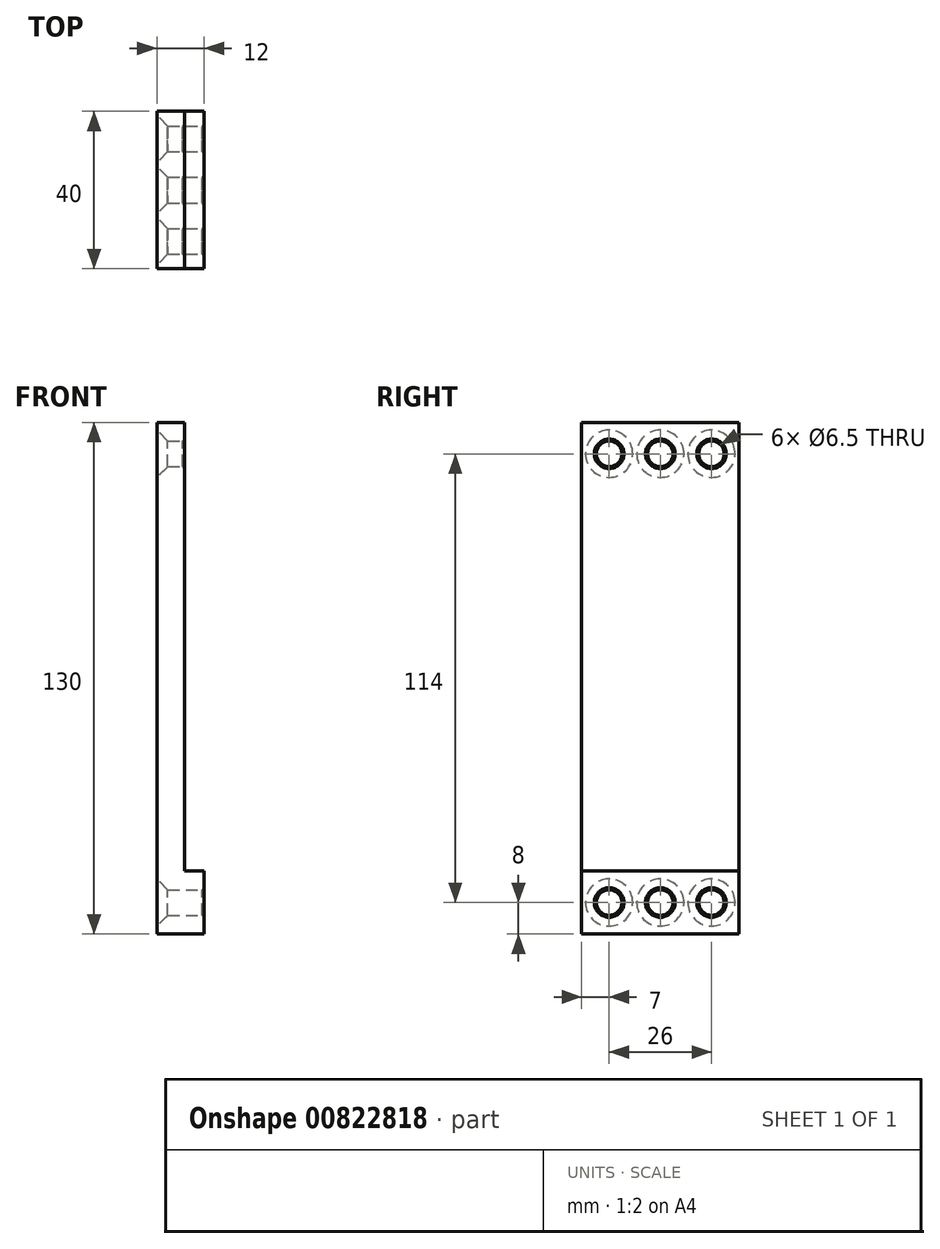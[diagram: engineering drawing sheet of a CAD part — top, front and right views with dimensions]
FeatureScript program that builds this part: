
annotation { "Feature Type Name" : "Feature", "Feature Type Description" : "" }
export const myFeature = defineFeature(function(context is Context, id is Id, definition is map)
    precondition{}
    {
        {
            var Q0;
            Q0=qCreatedBy(makeId("Right.planeOp"),FACE);
            var sketch = newSketch(context, id + "F0", { "sketchPlane" : qUnion([Q0])});
            skLineSegment(sketch, "E0", {"start": v(0, 0) * mm, "end": v(-13, 0) * mm, "construction": true});
            skLineSegment(sketch, "E1", {"start": v(0, 0) * mm, "end": v(0, 114) * mm, "construction": true});
            skLineSegment(sketch, "E2", {"start": v(0, 114) * mm, "end": v(-13, 114) * mm, "construction": true});
            skLineSegment(sketch, "E3", {"start": v(-13, 114) * mm, "end": v(-13, 0) * mm, "construction": true});
            skLineSegment(sketch, "E4.bottom", {"start": v(20, -8) * mm, "end": v(-20, -8) * mm});
            skLineSegment(sketch, "E4.top", {"start": v(20, 122) * mm, "end": v(-20, 122) * mm});
            skLineSegment(sketch, "E4.left", {"start": v(20, -8) * mm, "end": v(20, 122) * mm});
            skLineSegment(sketch, "E4.right", {"start": v(-20, -8) * mm, "end": v(-20, 122) * mm});
            skPoint(sketch, "E4.middle", {"position": v(0, 57) * mm});
            skCircle(sketch, "E5", {"center": v(0, 114) * mm, "radius": 3.25 * mm});
            skCircle(sketch, "E6", {"center": v(-13, 114) * mm, "radius": 3.25 * mm});
            skCircle(sketch, "E7", {"center": v(-13, 0) * mm, "radius": 3.25 * mm});
            skCircle(sketch, "E8", {"center": v(0, 0) * mm, "radius": 3.25 * mm});
            skCircle(sketch, "E9.MirrorC", {"center": v(13, 0) * mm, "radius": 3.25 * mm});
            skCircle(sketch, "E10.MirrorC", {"center": v(13, 114) * mm, "radius": 3.25 * mm});
            skSolve(sketch);
        }
        {
            var Q0;
            Q0 = qSketchRegion(id + "F0", true);
            extrude(context, id + "F1", {"entities" : qUnion([Q0]), "oppositeDirection" : true, "depth" : 7 * mm, "offsetDistance" : 25 * mm});
        }
        {
            var Q0;
            Q0=makeQuery(id+"F1.opExtrude","CAP_FACE",FACE,{"disambiguationData":[OSD([sQuery(id+"F0.wireOp",EDGE,"E4.bottom"),sQuery(id+"F0.wireOp",EDGE,"E4.top"),sQuery(id+"F0.wireOp",EDGE,"E4.left"),sQuery(id+"F0.wireOp",EDGE,"E4.right"),sQuery(id+"F0.wireOp",EDGE,"E5"),sQuery(id+"F0.wireOp",EDGE,"E6"),sQuery(id+"F0.wireOp",EDGE,"E7"),sQuery(id+"F0.wireOp",EDGE,"E8"),sQuery(id+"F0.wireOp",EDGE,"E9.MirrorC"),sQuery(id+"F0.wireOp",EDGE,"E10.MirrorC")])],"isStart":true});
            var sketch = newSketch(context, id + "F2", { "sketchPlane" : qUnion([Q0])});
            skCircle(sketch, "E11.0", {"center": v(-13, 0) * mm, "radius": 3.25 * mm});
            skLineSegment(sketch, "E12.0", {"start": v(20, -8) * mm, "end": v(-20, -8) * mm});
            skCircle(sketch, "E13.0", {"center": v(0, 0) * mm, "radius": 3.25 * mm});
            skCircle(sketch, "E14.0", {"center": v(13, 0) * mm, "radius": 3.25 * mm});
            skLineSegment(sketch, "E15", {"start": v(-20, -8) * mm, "end": v(-20, 8) * mm});
            skLineSegment(sketch, "E16", {"start": v(-20, 8) * mm, "end": v(20, 8) * mm});
            skLineSegment(sketch, "E17", {"start": v(20, 8) * mm, "end": v(20, -8) * mm});
            skSolve(sketch);
        }
        {
            var Q0;
            Q0 = qSketchRegion(id + "F2", true);
            extrude(context, id + "F3", {"entities" : qUnion([Q0]), "operationType" : NewBodyOperationType.ADD, "depth" : 5 * mm, "offsetDistance" : 25 * mm});
        }
        {
            var Q0;
            Q0=makeQuery(id+"F1.opExtrude","CAP_EDGE",EDGE,{"disambiguationData":[OSD([sQuery(id+"F0.wireOp",EDGE,"E7")])],"isStart":false});
            var Q1;
            Q1=makeQuery(id+"F1.opExtrude","CAP_EDGE",EDGE,{"disambiguationData":[OSD([sQuery(id+"F0.wireOp",EDGE,"E8")])],"isStart":false});
            var Q2;
            Q2=makeQuery(id+"F1.opExtrude","CAP_EDGE",EDGE,{"disambiguationData":[OSD([sQuery(id+"F0.wireOp",EDGE,"E9.MirrorC")])],"isStart":false});
            var Q3;
            Q3=makeQuery(id+"F1.opExtrude","CAP_EDGE",EDGE,{"disambiguationData":[OSD([sQuery(id+"F0.wireOp",EDGE,"E10.MirrorC")])],"isStart":false});
            var Q4;
            Q4=makeQuery(id+"F1.opExtrude","CAP_EDGE",EDGE,{"disambiguationData":[OSD([sQuery(id+"F0.wireOp",EDGE,"E5")])],"isStart":false});
            var Q5;
            Q5=makeQuery(id+"F1.opExtrude","CAP_EDGE",EDGE,{"disambiguationData":[OSD([sQuery(id+"F0.wireOp",EDGE,"E6")])],"isStart":false});
            chamfer(context, id + "F4", {"entities" : qUnion([Q0, Q1, Q2, Q3, Q4, Q5]), "width" : 2.75 * mm, "tangentPropagation" : true});
        }
        {
            var Q0;
            Q0=makeQuery(id+"F3.opExtrude","CAP_EDGE",EDGE,{"disambiguationData":[OSD([sQuery(id+"F2.wireOp",EDGE,"E11.0")])],"isStart":false});
            var Q1;
            Q1=makeQuery(id+"F3.opExtrude","CAP_EDGE",EDGE,{"disambiguationData":[OSD([sQuery(id+"F2.wireOp",EDGE,"E13.0")])],"isStart":false});
            var Q2;
            Q2=makeQuery(id+"F3.opExtrude","CAP_EDGE",EDGE,{"disambiguationData":[OSD([sQuery(id+"F2.wireOp",EDGE,"E14.0")])],"isStart":false});
            var Q3;
            Q3=makeQuery(id+"F1.opExtrude","CAP_EDGE",EDGE,{"disambiguationData":[OSD([sQuery(id+"F0.wireOp",EDGE,"E6")])],"isStart":true});
            var Q4;
            Q4=makeQuery(id+"F1.opExtrude","CAP_EDGE",EDGE,{"disambiguationData":[OSD([sQuery(id+"F0.wireOp",EDGE,"E5")])],"isStart":true});
            var Q5;
            Q5=makeQuery(id+"F1.opExtrude","CAP_EDGE",EDGE,{"disambiguationData":[OSD([sQuery(id+"F0.wireOp",EDGE,"E10.MirrorC")])],"isStart":true});
            chamfer(context, id + "F5", {"entities" : qUnion([Q0, Q1, Q2, Q3, Q4, Q5]), "width" : 0.5 * mm, "tangentPropagation" : true});
        }
    });
